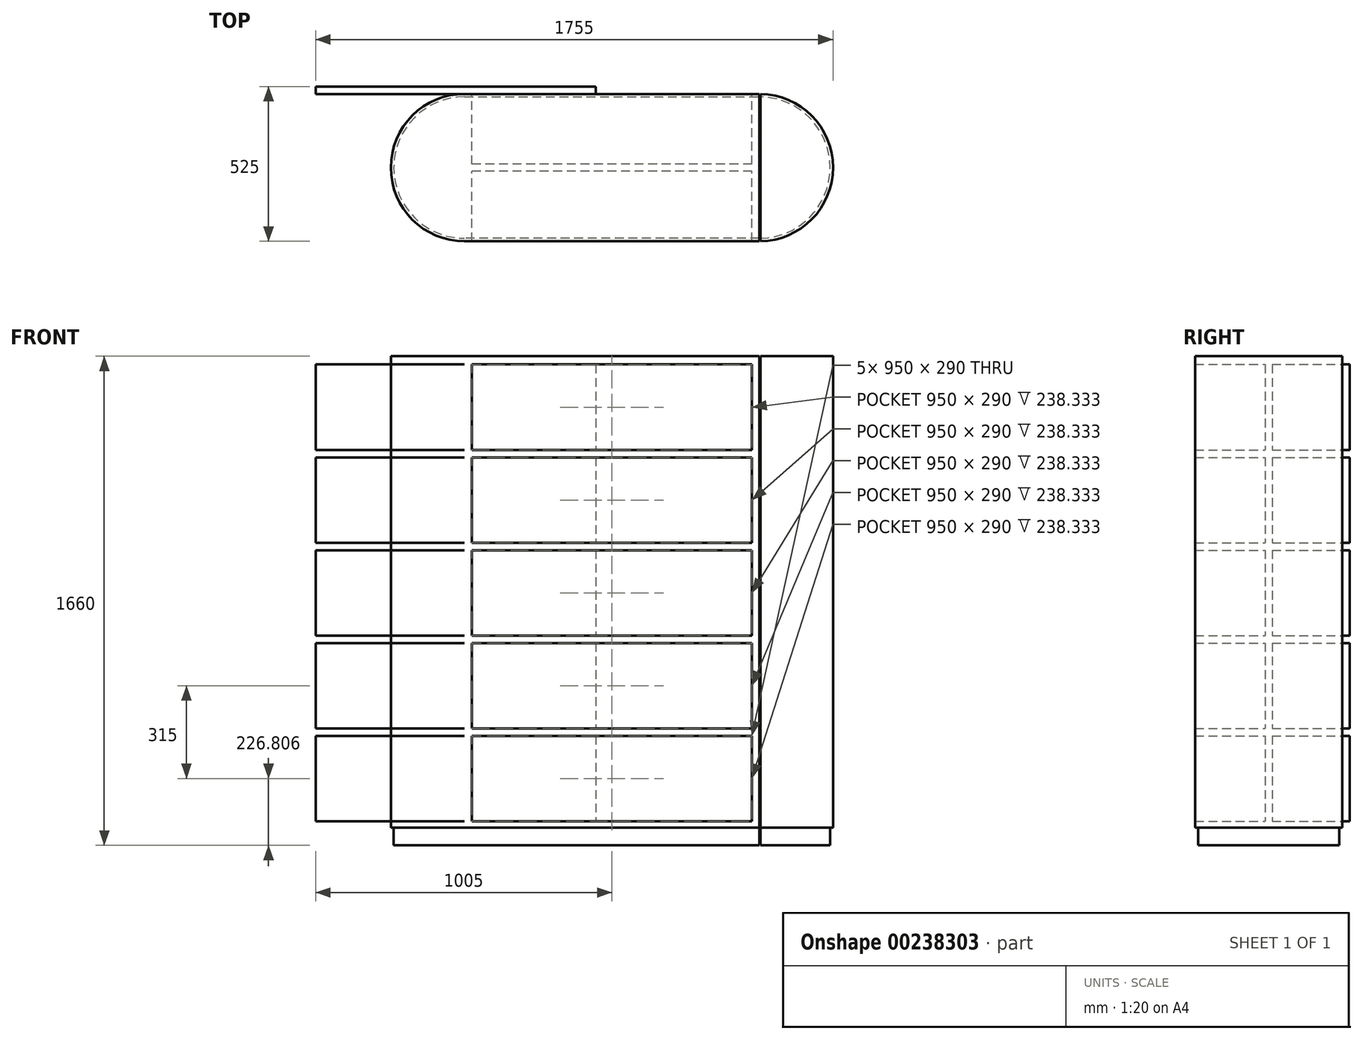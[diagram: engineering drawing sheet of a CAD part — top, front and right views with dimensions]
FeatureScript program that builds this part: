
annotation { "Feature Type Name" : "Feature", "Feature Type Description" : "" }
export const myFeature = defineFeature(function(context is Context, id is Id, definition is map)
    precondition{}
    {
        {
            var Q0;
            Q0=qCreatedBy(makeId("Top.planeOp"),FACE);
            var sketch = newSketch(context, id + "F0", { "sketchPlane" : qUnion([Q0])});
            skLineSegment(sketch, "E0.bottom", {"start": v(-500, 250) * mm, "end": v(500, 250) * mm});
            skLineSegment(sketch, "E0.top", {"start": v(-500, -250) * mm, "end": v(500, -250) * mm});
            skPoint(sketch, "E0.middle", {"position": v(0, 0) * mm});
            skArc(sketch, "E1", {"start": v(-500, 250) * mm, "mid": v(-750, 0) * mm, "end": v(-500, -250) * mm});
            skArc(sketch, "E2", {"start": v(500, -250) * mm, "mid": v(750, 0) * mm, "end": v(500, 250) * mm});
            skSolve(sketch);
        }
        {
            var Q0;
            Q0=makeQuery(id+"F0.imprint","IMPRINT",FACE,{"disambiguationData":[TD([[makeQuery(id+"F0.imprint","IMPRINT",EDGE,{"derivedFrom":sQuery(id+"F0.wireOp",EDGE,"E0.bottom")}),-1.0]])]});
            extrude(context, id + "F1", {"entities" : qUnion([Q0]), "depth" : 1600 * mm});
        }
        {
            var Q0;
            Q0=makeQuery(id+"F1.opExtrude","SWEPT_FACE",FACE,{"disambiguationData":[OSD([sQuery(id+"F0.wireOp",EDGE,"E0.bottom")])]});
            var sketch = newSketch(context, id + "F2", { "sketchPlane" : qUnion([Q0])});
            skLineSegment(sketch, "E3.0", {"start": v(-475, 1571.8) * mm, "end": v(475, 1571.8) * mm});
            skLineSegment(sketch, "E3.1", {"start": v(-475, 1571.8) * mm, "end": v(-475, 1281.8) * mm});
            skLineSegment(sketch, "E3.3", {"start": v(475, 1571.8) * mm, "end": v(475, 1281.8) * mm});
            skLineSegment(sketch, "E4", {"start": v(-475, 1281.8) * mm, "end": v(475, 1281.8) * mm});
            skLineSegment(sketch, "E5.0.1.0", {"start": v(-475, 1256.8) * mm, "end": v(475, 1256.8) * mm});
            skLineSegment(sketch, "E5.0.1.1", {"start": v(-475, 1256.8) * mm, "end": v(-475, 966.8) * mm});
            skLineSegment(sketch, "E5.0.1.2", {"start": v(-475, 966.8) * mm, "end": v(475, 966.8) * mm});
            skLineSegment(sketch, "E5.0.1.3", {"start": v(475, 1256.8) * mm, "end": v(475, 966.8) * mm});
            skLineSegment(sketch, "E5.0.2.0", {"start": v(-475, 941.8) * mm, "end": v(475, 941.8) * mm});
            skLineSegment(sketch, "E5.0.2.1", {"start": v(-475, 941.8) * mm, "end": v(-475, 651.8) * mm});
            skLineSegment(sketch, "E5.0.2.2", {"start": v(-475, 651.8) * mm, "end": v(475, 651.8) * mm});
            skLineSegment(sketch, "E5.0.2.3", {"start": v(475, 941.8) * mm, "end": v(475, 651.8) * mm});
            skLineSegment(sketch, "E5.0.3.0", {"start": v(-475, 626.8) * mm, "end": v(475, 626.8) * mm});
            skLineSegment(sketch, "E5.0.3.1", {"start": v(-475, 626.8) * mm, "end": v(-475, 336.8) * mm});
            skLineSegment(sketch, "E5.0.3.2", {"start": v(-475, 336.8) * mm, "end": v(475, 336.8) * mm});
            skLineSegment(sketch, "E5.0.3.3", {"start": v(475, 626.8) * mm, "end": v(475, 336.8) * mm});
            skLineSegment(sketch, "E5.0.4.0", {"start": v(-475, 311.8) * mm, "end": v(475, 311.8) * mm});
            skLineSegment(sketch, "E5.0.4.1", {"start": v(-475, 311.8) * mm, "end": v(-475, 21.8) * mm});
            skLineSegment(sketch, "E5.0.4.2", {"start": v(-475, 21.8) * mm, "end": v(475, 21.8) * mm});
            skLineSegment(sketch, "E5.0.4.3", {"start": v(475, 311.8) * mm, "end": v(475, 21.8) * mm});
            skLineSegment(sketch, "E5.1.1.0", {"start": v(-475, 1256.8) * mm, "end": v(475, 1256.8) * mm});
            skLineSegment(sketch, "E5.1.1.1", {"start": v(-475, 1256.8) * mm, "end": v(-475, 966.8) * mm});
            skLineSegment(sketch, "E5.1.1.2", {"start": v(-475, 966.8) * mm, "end": v(475, 966.8) * mm});
            skLineSegment(sketch, "E5.1.1.3", {"start": v(475, 1256.8) * mm, "end": v(475, 966.8) * mm});
            skLineSegment(sketch, "E5.1.2.0", {"start": v(-475, 941.8) * mm, "end": v(475, 941.8) * mm});
            skLineSegment(sketch, "E5.1.2.1", {"start": v(-475, 941.8) * mm, "end": v(-475, 651.8) * mm});
            skLineSegment(sketch, "E5.1.2.2", {"start": v(-475, 651.8) * mm, "end": v(475, 651.8) * mm});
            skLineSegment(sketch, "E5.1.2.3", {"start": v(475, 941.8) * mm, "end": v(475, 651.8) * mm});
            skLineSegment(sketch, "E5.1.3.0", {"start": v(-475, 626.8) * mm, "end": v(475, 626.8) * mm});
            skLineSegment(sketch, "E5.1.3.1", {"start": v(-475, 626.8) * mm, "end": v(-475, 336.8) * mm});
            skLineSegment(sketch, "E5.1.3.2", {"start": v(-475, 336.8) * mm, "end": v(475, 336.8) * mm});
            skLineSegment(sketch, "E5.1.3.3", {"start": v(475, 626.8) * mm, "end": v(475, 336.8) * mm});
            skLineSegment(sketch, "E5.1.4.0", {"start": v(-475, 311.8) * mm, "end": v(475, 311.8) * mm});
            skLineSegment(sketch, "E5.1.4.1", {"start": v(-475, 311.8) * mm, "end": v(-475, 21.8) * mm});
            skLineSegment(sketch, "E5.1.4.2", {"start": v(-475, 21.8) * mm, "end": v(475, 21.8) * mm});
            skLineSegment(sketch, "E5.1.4.3", {"start": v(475, 311.8) * mm, "end": v(475, 21.8) * mm});
            skLineSegment(sketch, "E5.2.1.0", {"start": v(-475, 1256.8) * mm, "end": v(475, 1256.8) * mm});
            skLineSegment(sketch, "E5.2.1.1", {"start": v(-475, 1256.8) * mm, "end": v(-475, 966.8) * mm});
            skLineSegment(sketch, "E5.2.1.2", {"start": v(-475, 966.8) * mm, "end": v(475, 966.8) * mm});
            skLineSegment(sketch, "E5.2.1.3", {"start": v(475, 1256.8) * mm, "end": v(475, 966.8) * mm});
            skLineSegment(sketch, "E5.2.2.0", {"start": v(-475, 941.8) * mm, "end": v(475, 941.8) * mm});
            skLineSegment(sketch, "E5.2.2.1", {"start": v(-475, 941.8) * mm, "end": v(-475, 651.8) * mm});
            skLineSegment(sketch, "E5.2.2.2", {"start": v(-475, 651.8) * mm, "end": v(475, 651.8) * mm});
            skLineSegment(sketch, "E5.2.2.3", {"start": v(475, 941.8) * mm, "end": v(475, 651.8) * mm});
            skLineSegment(sketch, "E5.2.3.0", {"start": v(-475, 626.8) * mm, "end": v(475, 626.8) * mm});
            skLineSegment(sketch, "E5.2.3.1", {"start": v(-475, 626.8) * mm, "end": v(-475, 336.8) * mm});
            skLineSegment(sketch, "E5.2.3.2", {"start": v(-475, 336.8) * mm, "end": v(475, 336.8) * mm});
            skLineSegment(sketch, "E5.2.3.3", {"start": v(475, 626.8) * mm, "end": v(475, 336.8) * mm});
            skLineSegment(sketch, "E5.2.4.0", {"start": v(-475, 311.8) * mm, "end": v(475, 311.8) * mm});
            skLineSegment(sketch, "E5.2.4.1", {"start": v(-475, 311.8) * mm, "end": v(-475, 21.8) * mm});
            skLineSegment(sketch, "E5.2.4.2", {"start": v(-475, 21.8) * mm, "end": v(475, 21.8) * mm});
            skLineSegment(sketch, "E5.2.4.3", {"start": v(475, 311.8) * mm, "end": v(475, 21.8) * mm});
            skLineSegment(sketch, "E5.direction1", {"start": v(-475, 1281.8) * mm, "end": v(-475, 1281.8) * mm});
            skLineSegment(sketch, "E5.direction2", {"start": v(-475, 1281.8) * mm, "end": v(-475, 966.8) * mm, "construction": true});
            skSolve(sketch);
        }
        {
            var Q0;
            Q0 = qSketchRegion(id + "F2", true);
            extrude(context, id + "F3", {"entities" : qUnion([Q0]), "operationType" : NewBodyOperationType.REMOVE, "endBound" : BoundingType.THROUGH_ALL, "oppositeDirection" : true, "depth" : 25 * mm});
        }
        {
            var Q0;
            Q0=makeQuery(id+"F1.opExtrude","CAP_FACE",FACE,{"disambiguationData":[OSD([sQuery(id+"F0.wireOp",EDGE,"E0.bottom"),sQuery(id+"F0.wireOp",EDGE,"E0.top"),sQuery(id+"F0.wireOp",EDGE,"E1"),sQuery(id+"F0.wireOp",EDGE,"E2")])],"isStart":false});
            var sketch = newSketch(context, id + "F4", { "sketchPlane" : qUnion([Q0])});
            skLineSegment(sketch, "E6.bottom", {"start": v(-624.17, 11.67) * mm, "end": v(624.17, 11.67) * mm});
            skLineSegment(sketch, "E6.top", {"start": v(-624.17, -11.67) * mm, "end": v(624.17, -11.67) * mm});
            skLineSegment(sketch, "E6.left", {"start": v(-624.17, 11.67) * mm, "end": v(-624.17, -11.67) * mm});
            skLineSegment(sketch, "E6.right", {"start": v(624.17, 11.67) * mm, "end": v(624.17, -11.67) * mm});
            skPoint(sketch, "E6.middle", {"position": v(0, 0) * mm});
            skSolve(sketch);
        }
        {
            var Q0;
            Q0 = qSketchRegion(id + "F4", true);
            var Q1;
            Q1=makeQuery(id+"F1.opExtrude","CAP_FACE",FACE,{"disambiguationData":[OSD([sQuery(id+"F0.wireOp",EDGE,"E0.bottom"),sQuery(id+"F0.wireOp",EDGE,"E0.top"),sQuery(id+"F0.wireOp",EDGE,"E1"),sQuery(id+"F0.wireOp",EDGE,"E2")])],"isStart":true});
            extrude(context, id + "F5", {"entities" : qUnion([Q0]), "operationType" : NewBodyOperationType.ADD, "endBound" : BoundingType.UP_TO_SURFACE, "oppositeDirection" : true, "endBoundEntityFace" : qUnion([Q1]), "depth" : 25 * mm});
        }
        {
            var Q0;
            Q0=makeQuery(id+"F1.opExtrude","CAP_FACE",FACE,{"disambiguationData":[OSD([sQuery(id+"F0.wireOp",EDGE,"E0.bottom"),sQuery(id+"F0.wireOp",EDGE,"E0.top"),sQuery(id+"F0.wireOp",EDGE,"E1"),sQuery(id+"F0.wireOp",EDGE,"E2")])],"isStart":true});
            var sketch = newSketch(context, id + "F6", { "sketchPlane" : qUnion([Q0])});
            skArc(sketch, "E7.0", {"start": v(-500, 240) * mm, "mid": v(-740, 0) * mm, "end": v(-500, -240) * mm});
            skLineSegment(sketch, "E7.1", {"start": v(500, 240) * mm, "end": v(-500, 240) * mm});
            skArc(sketch, "E7.2", {"start": v(500, -240) * mm, "mid": v(740, 0) * mm, "end": v(500, 240) * mm});
            skLineSegment(sketch, "E7.3", {"start": v(-500, -240) * mm, "end": v(500, -240) * mm});
            skSolve(sketch);
        }
        {
            var Q0;
            Q0 = qSketchRegion(id + "F6", true);
            extrude(context, id + "F7", {"entities" : qUnion([Q0]), "operationType" : NewBodyOperationType.ADD, "depth" : 60 * mm});
        }
        {
            var Q0;
            Q0 = qSketchRegion(id + "F2", true);
            extrude(context, id + "F8", {"entities" : qUnion([Q0]), "operationType" : NewBodyOperationType.ADD, "depth" : 25 * mm});
        }
        {
            var Q0;
            Q0=makeQuery(id+"F1.opExtrude","CAP_FACE",FACE,{"disambiguationData":[OSD([sQuery(id+"F0.wireOp",EDGE,"E0.bottom"),sQuery(id+"F0.wireOp",EDGE,"E0.top"),sQuery(id+"F0.wireOp",EDGE,"E1"),sQuery(id+"F0.wireOp",EDGE,"E2")])],"isStart":false});
            var sketch = newSketch(context, id + "F9", { "sketchPlane" : qUnion([Q0])});
            skLineSegment(sketch, "E8.bottom", {"start": v(500, 250) * mm, "end": v(503.75, 250) * mm});
            skLineSegment(sketch, "E8.top", {"start": v(500, -293.36) * mm, "end": v(503.75, -293.36) * mm});
            skLineSegment(sketch, "E8.left", {"start": v(500, 250) * mm, "end": v(500, -293.36) * mm});
            skLineSegment(sketch, "E8.right", {"start": v(503.75, 250) * mm, "end": v(503.75, -293.36) * mm});
            skSolve(sketch);
        }
        {
            var Q0;
            Q0 = qSketchRegion(id + "F9", true);
            extrude(context, id + "F10", {"entities" : qUnion([Q0]), "operationType" : NewBodyOperationType.REMOVE, "endBound" : BoundingType.THROUGH_ALL, "oppositeDirection" : true, "depth" : 25 * mm});
        }
        {
            var Q0;
            Q0=makeQuery(id+"F10.boolean.opBoolean","SPLIT",BODY,{"disambiguationData":[OD(1.0)],"derivedFrom":makeQuery(id+"F1.opExtrude","SWEPT_BODY",BODY,{"disambiguationData":[OSD([sQuery(id+"F0.wireOp",EDGE,"E0.bottom"),sQuery(id+"F0.wireOp",EDGE,"E0.top"),sQuery(id+"F0.wireOp",EDGE,"E1"),sQuery(id+"F0.wireOp",EDGE,"E2")])]})});
            transform(context, id + "F11", {"entities" : qUnion([Q0]), "transformType" : TransformType.TRANSLATION_3D, "dx" : 530 * mm, "dy" : 0 * mm, "dz" : 0 * mm, "makeCopy" : false});
        }
    });
